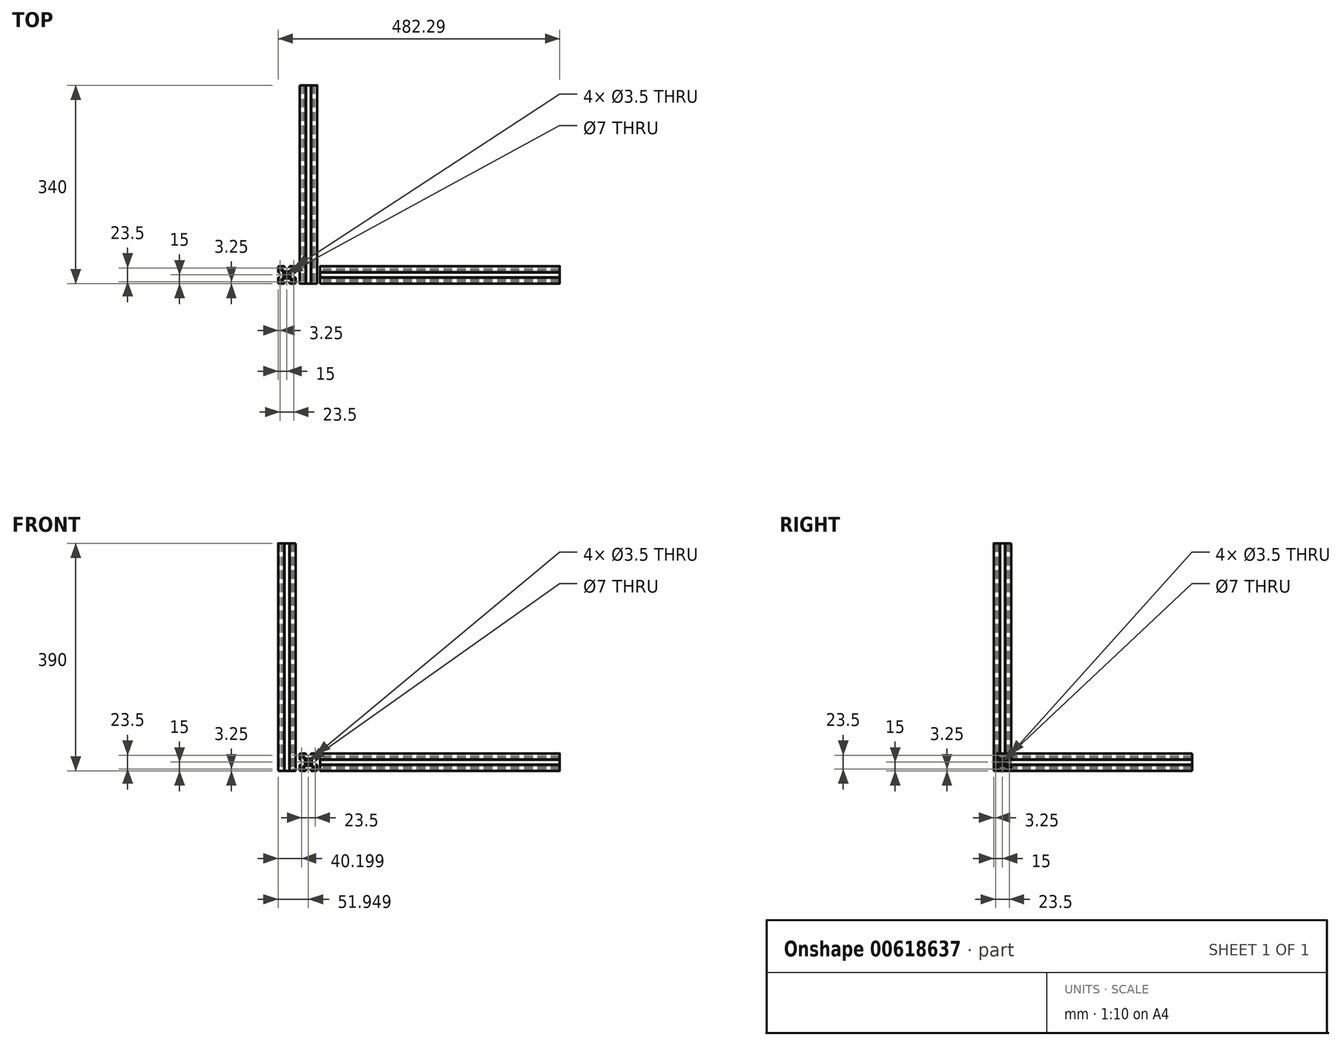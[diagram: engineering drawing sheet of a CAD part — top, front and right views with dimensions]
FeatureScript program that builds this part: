
annotation { "Feature Type Name" : "Feature", "Feature Type Description" : "" }
export const myFeature = defineFeature(function(context is Context, id is Id, definition is map)
    precondition{}
    {
        {
            var Q0;
            Q0=qCreatedBy(makeId("Front.planeOp"),FACE);
            var sketch = newSketch(context, id + "F0", { "sketchPlane" : qUnion([Q0])});
            skLineSegment(sketch, "E0.bottom", {"start": v(-33.34, 30) * mm, "end": v(-25.04, 30) * mm});
            skLineSegment(sketch, "E0.top", {"start": v(-33.34, 0) * mm, "end": v(-25.04, 0) * mm});
            skLineSegment(sketch, "E0.left", {"start": v(-35.34, 28) * mm, "end": v(-35.34, 19.7) * mm});
            skLineSegment(sketch, "E0.right", {"start": v(-5.34, 28) * mm, "end": v(-5.34, 19.7) * mm});
            skPoint(sketch, "E1", {"position": v(-20.34, 15) * mm});
            skLineSegment(sketch, "E2.bottom", {"start": v(-28.84, 27.8) * mm, "end": v(-24.44, 27.8) * mm});
            skLineSegment(sketch, "E2.left", {"start": v(-33.14, 23.5) * mm, "end": v(-33.14, 19.1) * mm});
            skCircle(sketch, "E3", {"center": v(-20.34, 15) * mm, "radius": 3.5 * mm});
            skCircle(sketch, "E4", {"center": v(-32.1, 3.25) * mm, "radius": 1.75 * mm});
            skCircle(sketch, "E5", {"center": v(-32.1, 26.75) * mm, "radius": 1.75 * mm});
            skCircle(sketch, "E6", {"center": v(-8.6, 26.75) * mm, "radius": 1.75 * mm});
            skCircle(sketch, "E7", {"center": v(-8.6, 3.25) * mm, "radius": 1.75 * mm});
            skLineSegment(sketch, "E8.right", {"start": v(-16.24, 2.2) * mm, "end": v(-16.24, 0.5) * mm});
            skLineSegment(sketch, "E9.trimOffspring", {"start": v(-16.24, 2.2) * mm, "end": v(-11.84, 2.2) * mm});
            skLineSegment(sketch, "E10.trimOffspring", {"start": v(-15.64, 0) * mm, "end": v(-7.34, 0) * mm});
            skLineSegment(sketch, "E11.trimOffspring", {"start": v(-24.44, 2.2) * mm, "end": v(-24.44, 0.5) * mm});
            skLineSegment(sketch, "E12.trimOffspring", {"start": v(-28.84, 2.2) * mm, "end": v(-24.44, 2.2) * mm});
            skLineSegment(sketch, "E13.trimOffspring", {"start": v(-7.54, 23.5) * mm, "end": v(-7.54, 19.1) * mm});
            skLineSegment(sketch, "E14", {"start": v(-24.44, 27.8) * mm, "end": v(-24.44, 29.5) * mm});
            skLineSegment(sketch, "E15", {"start": v(-16.24, 27.8) * mm, "end": v(-16.24, 29.5) * mm});
            skLineSegment(sketch, "E16.trimOffspring", {"start": v(-15.64, 30) * mm, "end": v(-7.34, 30) * mm});
            skLineSegment(sketch, "E17.trimOffspring", {"start": v(-16.24, 27.8) * mm, "end": v(-11.84, 27.8) * mm});
            skLineSegment(sketch, "E18", {"start": v(-7.54, 10.9) * mm, "end": v(-5.84, 10.9) * mm});
            skLineSegment(sketch, "E19", {"start": v(-7.54, 19.1) * mm, "end": v(-5.84, 19.1) * mm});
            skLineSegment(sketch, "E20", {"start": v(-33.14, 10.9) * mm, "end": v(-34.84, 10.9) * mm});
            skLineSegment(sketch, "E21", {"start": v(-33.14, 19.1) * mm, "end": v(-34.84, 19.1) * mm});
            skLineSegment(sketch, "E22.trimOffspring", {"start": v(-5.34, 10.3) * mm, "end": v(-5.34, 2) * mm});
            skLineSegment(sketch, "E23.trimOffspring", {"start": v(-7.54, 10.9) * mm, "end": v(-7.54, 6.5) * mm});
            skLineSegment(sketch, "E24.trimOffspring", {"start": v(-33.14, 10.9) * mm, "end": v(-33.14, 6.5) * mm});
            skLineSegment(sketch, "E25.trimOffspring", {"start": v(-35.34, 10.3) * mm, "end": v(-35.34, 2) * mm});
            skLineSegment(sketch, "E26.bottom", {"start": v(-24.93, 21) * mm, "end": v(-15.75, 21) * mm});
            skLineSegment(sketch, "E26.top", {"start": v(-24.93, 9) * mm, "end": v(-15.75, 9) * mm});
            skLineSegment(sketch, "E26.left", {"start": v(-26.34, 19.59) * mm, "end": v(-26.34, 10.41) * mm});
            skLineSegment(sketch, "E26.right", {"start": v(-14.34, 19.59) * mm, "end": v(-14.34, 10.41) * mm});
            skLineSegment(sketch, "E27", {"start": v(-28.84, 27.8) * mm, "end": v(-28.84, 24.91) * mm});
            skLineSegment(sketch, "E28", {"start": v(-30.25, 23.5) * mm, "end": v(-33.14, 23.5) * mm});
            skLineSegment(sketch, "E29", {"start": v(-11.84, 24.91) * mm, "end": v(-11.84, 27.8) * mm});
            skLineSegment(sketch, "E30", {"start": v(-10.43, 23.5) * mm, "end": v(-7.54, 23.5) * mm});
            skLineSegment(sketch, "E31", {"start": v(-10.43, 6.5) * mm, "end": v(-7.54, 6.5) * mm});
            skLineSegment(sketch, "E32", {"start": v(-11.84, 5.09) * mm, "end": v(-11.84, 2.2) * mm});
            skLineSegment(sketch, "E33", {"start": v(-28.84, 5.09) * mm, "end": v(-28.84, 2.2) * mm});
            skLineSegment(sketch, "E34", {"start": v(-30.25, 6.5) * mm, "end": v(-33.14, 6.5) * mm});
            skLineSegment(sketch, "E35", {"start": v(-30.25, 23.5) * mm, "end": v(-26.34, 19.59) * mm});
            skLineSegment(sketch, "E36", {"start": v(-28.84, 24.91) * mm, "end": v(-24.93, 21) * mm});
            skLineSegment(sketch, "E37", {"start": v(-14.34, 10.41) * mm, "end": v(-10.43, 6.5) * mm});
            skLineSegment(sketch, "E38", {"start": v(-15.75, 9) * mm, "end": v(-11.84, 5.09) * mm});
            skLineSegment(sketch, "E39", {"start": v(-28.84, 5.09) * mm, "end": v(-24.93, 9) * mm});
            skLineSegment(sketch, "E40", {"start": v(-30.25, 6.5) * mm, "end": v(-26.34, 10.41) * mm});
            skLineSegment(sketch, "E41", {"start": v(-15.75, 21) * mm, "end": v(-11.84, 24.91) * mm});
            skLineSegment(sketch, "E42", {"start": v(-14.34, 19.59) * mm, "end": v(-10.43, 23.5) * mm});
            skArc(sketch, "E43.filletArc", {"start": v(-33.34, 30) * mm, "mid": v(-34.75, 29.41) * mm, "end": v(-35.34, 28) * mm});
            skArc(sketch, "E44.filletArc", {"start": v(-5.34, 28) * mm, "mid": v(-5.93, 29.41) * mm, "end": v(-7.34, 30) * mm});
            skArc(sketch, "E45.filletArc", {"start": v(-7.34, 0) * mm, "mid": v(-5.93, 0.59) * mm, "end": v(-5.34, 2) * mm});
            skArc(sketch, "E46.filletArc", {"start": v(-35.34, 2) * mm, "mid": v(-34.75, 0.59) * mm, "end": v(-33.34, 0) * mm});
            skLineSegment(sketch, "E47", {"start": v(-5.84, 19.1) * mm, "end": v(-5.84, 19.7) * mm});
            skLineSegment(sketch, "E48", {"start": v(-5.84, 19.7) * mm, "end": v(-5.34, 19.7) * mm});
            skLineSegment(sketch, "E49.top", {"start": v(-5.34, 10.3) * mm, "end": v(-5.84, 10.3) * mm});
            skLineSegment(sketch, "E49.right", {"start": v(-5.84, 10.9) * mm, "end": v(-5.84, 10.3) * mm});
            skLineSegment(sketch, "E50.top", {"start": v(-16.24, 0.5) * mm, "end": v(-15.64, 0.5) * mm});
            skLineSegment(sketch, "E50.right", {"start": v(-15.64, 0) * mm, "end": v(-15.64, 0.5) * mm});
            skLineSegment(sketch, "E51.top", {"start": v(-24.44, 0.5) * mm, "end": v(-25.04, 0.5) * mm});
            skLineSegment(sketch, "E51.right", {"start": v(-25.04, 0) * mm, "end": v(-25.04, 0.5) * mm});
            skLineSegment(sketch, "E52.top", {"start": v(-35.34, 10.3) * mm, "end": v(-34.84, 10.3) * mm});
            skLineSegment(sketch, "E52.right", {"start": v(-34.84, 10.9) * mm, "end": v(-34.84, 10.3) * mm});
            skLineSegment(sketch, "E53.top", {"start": v(-35.34, 19.7) * mm, "end": v(-34.84, 19.7) * mm});
            skLineSegment(sketch, "E53.right", {"start": v(-34.84, 19.1) * mm, "end": v(-34.84, 19.7) * mm});
            skLineSegment(sketch, "E54.top", {"start": v(-24.44, 29.5) * mm, "end": v(-25.04, 29.5) * mm});
            skLineSegment(sketch, "E54.right", {"start": v(-25.04, 30) * mm, "end": v(-25.04, 29.5) * mm});
            skLineSegment(sketch, "E55.top", {"start": v(-16.24, 29.5) * mm, "end": v(-15.64, 29.5) * mm});
            skLineSegment(sketch, "E55.right", {"start": v(-15.64, 30) * mm, "end": v(-15.64, 29.5) * mm});
            skSolve(sketch);
        }
        {
            var Q0;
            Q0 = qSketchRegion(id + "F0", true);
            extrude(context, id + "F1", {"entities" : qUnion([Q0]), "oppositeDirection" : true, "depth" : 340 * mm, "offsetDistance" : 25 * mm});
        }
        {
            var Q0;
            Q0=qCreatedBy(makeId("Top.planeOp"),FACE);
            var sketch = newSketch(context, id + "F2", { "sketchPlane" : qUnion([Q0])});
            skLineSegment(sketch, "E56.bottom", {"start": v(-70.29, 30) * mm, "end": v(-61.99, 30) * mm});
            skLineSegment(sketch, "E56.top", {"start": v(-70.29, 0) * mm, "end": v(-61.99, 0) * mm});
            skLineSegment(sketch, "E56.left", {"start": v(-72.29, 28) * mm, "end": v(-72.29, 19.7) * mm});
            skLineSegment(sketch, "E56.right", {"start": v(-42.29, 28) * mm, "end": v(-42.29, 19.7) * mm});
            skPoint(sketch, "E57", {"position": v(-57.29, 15) * mm});
            skLineSegment(sketch, "E58.bottom", {"start": v(-65.79, 27.8) * mm, "end": v(-61.39, 27.8) * mm});
            skLineSegment(sketch, "E58.left", {"start": v(-70.09, 23.5) * mm, "end": v(-70.09, 19.1) * mm});
            skCircle(sketch, "E59", {"center": v(-57.29, 15) * mm, "radius": 3.5 * mm});
            skCircle(sketch, "E60", {"center": v(-69.04, 3.25) * mm, "radius": 1.75 * mm});
            skCircle(sketch, "E61", {"center": v(-69.04, 26.75) * mm, "radius": 1.75 * mm});
            skCircle(sketch, "E62", {"center": v(-45.54, 26.75) * mm, "radius": 1.75 * mm});
            skCircle(sketch, "E63", {"center": v(-45.54, 3.25) * mm, "radius": 1.75 * mm});
            skLineSegment(sketch, "E64.right", {"start": v(-53.19, 2.2) * mm, "end": v(-53.19, 0.5) * mm});
            skLineSegment(sketch, "E65.trimOffspring", {"start": v(-53.19, 2.2) * mm, "end": v(-48.79, 2.2) * mm});
            skLineSegment(sketch, "E66.trimOffspring", {"start": v(-52.59, 0) * mm, "end": v(-44.29, 0) * mm});
            skLineSegment(sketch, "E67.trimOffspring", {"start": v(-61.39, 2.2) * mm, "end": v(-61.39, 0.5) * mm});
            skLineSegment(sketch, "E68.trimOffspring", {"start": v(-65.79, 2.2) * mm, "end": v(-61.39, 2.2) * mm});
            skLineSegment(sketch, "E69.trimOffspring", {"start": v(-44.49, 23.5) * mm, "end": v(-44.49, 19.1) * mm});
            skLineSegment(sketch, "E70", {"start": v(-61.39, 27.8) * mm, "end": v(-61.39, 29.5) * mm});
            skLineSegment(sketch, "E71", {"start": v(-53.19, 27.8) * mm, "end": v(-53.19, 29.5) * mm});
            skLineSegment(sketch, "E72.trimOffspring", {"start": v(-52.59, 30) * mm, "end": v(-44.29, 30) * mm});
            skLineSegment(sketch, "E73.trimOffspring", {"start": v(-53.19, 27.8) * mm, "end": v(-48.79, 27.8) * mm});
            skLineSegment(sketch, "E74", {"start": v(-44.49, 10.9) * mm, "end": v(-42.79, 10.9) * mm});
            skLineSegment(sketch, "E75", {"start": v(-44.49, 19.1) * mm, "end": v(-42.79, 19.1) * mm});
            skLineSegment(sketch, "E76", {"start": v(-70.09, 10.9) * mm, "end": v(-71.79, 10.9) * mm});
            skLineSegment(sketch, "E77", {"start": v(-70.09, 19.1) * mm, "end": v(-71.79, 19.1) * mm});
            skLineSegment(sketch, "E78.trimOffspring", {"start": v(-42.29, 10.3) * mm, "end": v(-42.29, 2) * mm});
            skLineSegment(sketch, "E79.trimOffspring", {"start": v(-44.49, 10.9) * mm, "end": v(-44.49, 6.5) * mm});
            skLineSegment(sketch, "E80.trimOffspring", {"start": v(-70.09, 10.9) * mm, "end": v(-70.09, 6.5) * mm});
            skLineSegment(sketch, "E81.trimOffspring", {"start": v(-72.29, 10.3) * mm, "end": v(-72.29, 2) * mm});
            skLineSegment(sketch, "E82.bottom", {"start": v(-61.88, 21) * mm, "end": v(-52.7, 21) * mm});
            skLineSegment(sketch, "E82.top", {"start": v(-61.88, 9) * mm, "end": v(-52.7, 9) * mm});
            skLineSegment(sketch, "E82.left", {"start": v(-63.29, 19.59) * mm, "end": v(-63.29, 10.41) * mm});
            skLineSegment(sketch, "E82.right", {"start": v(-51.29, 19.59) * mm, "end": v(-51.29, 10.41) * mm});
            skLineSegment(sketch, "E83", {"start": v(-65.79, 27.8) * mm, "end": v(-65.79, 24.91) * mm});
            skLineSegment(sketch, "E84", {"start": v(-67.2, 23.5) * mm, "end": v(-70.09, 23.5) * mm});
            skLineSegment(sketch, "E85", {"start": v(-48.79, 24.91) * mm, "end": v(-48.79, 27.8) * mm});
            skLineSegment(sketch, "E86", {"start": v(-47.38, 23.5) * mm, "end": v(-44.49, 23.5) * mm});
            skLineSegment(sketch, "E87", {"start": v(-47.38, 6.5) * mm, "end": v(-44.49, 6.5) * mm});
            skLineSegment(sketch, "E88", {"start": v(-48.79, 5.09) * mm, "end": v(-48.79, 2.2) * mm});
            skLineSegment(sketch, "E89", {"start": v(-65.79, 5.09) * mm, "end": v(-65.79, 2.2) * mm});
            skLineSegment(sketch, "E90", {"start": v(-67.2, 6.5) * mm, "end": v(-70.09, 6.5) * mm});
            skLineSegment(sketch, "E91", {"start": v(-67.2, 23.5) * mm, "end": v(-63.29, 19.59) * mm});
            skLineSegment(sketch, "E92", {"start": v(-65.79, 24.91) * mm, "end": v(-61.88, 21) * mm});
            skLineSegment(sketch, "E93", {"start": v(-51.29, 10.41) * mm, "end": v(-47.38, 6.5) * mm});
            skLineSegment(sketch, "E94", {"start": v(-52.7, 9) * mm, "end": v(-48.79, 5.09) * mm});
            skLineSegment(sketch, "E95", {"start": v(-65.79, 5.09) * mm, "end": v(-61.88, 9) * mm});
            skLineSegment(sketch, "E96", {"start": v(-67.2, 6.5) * mm, "end": v(-63.29, 10.41) * mm});
            skLineSegment(sketch, "E97", {"start": v(-52.7, 21) * mm, "end": v(-48.79, 24.91) * mm});
            skLineSegment(sketch, "E98", {"start": v(-51.29, 19.59) * mm, "end": v(-47.38, 23.5) * mm});
            skArc(sketch, "E99.filletArc", {"start": v(-70.29, 30) * mm, "mid": v(-71.7, 29.41) * mm, "end": v(-72.29, 28) * mm});
            skArc(sketch, "E100.filletArc", {"start": v(-42.29, 28) * mm, "mid": v(-42.88, 29.41) * mm, "end": v(-44.29, 30) * mm});
            skArc(sketch, "E101.filletArc", {"start": v(-44.29, 0) * mm, "mid": v(-42.88, 0.59) * mm, "end": v(-42.29, 2) * mm});
            skArc(sketch, "E102.filletArc", {"start": v(-72.29, 2) * mm, "mid": v(-71.7, 0.59) * mm, "end": v(-70.29, 0) * mm});
            skLineSegment(sketch, "E103", {"start": v(-42.79, 19.1) * mm, "end": v(-42.79, 19.7) * mm});
            skLineSegment(sketch, "E104", {"start": v(-42.79, 19.7) * mm, "end": v(-42.29, 19.7) * mm});
            skLineSegment(sketch, "E105.top", {"start": v(-42.29, 10.3) * mm, "end": v(-42.79, 10.3) * mm});
            skLineSegment(sketch, "E105.right", {"start": v(-42.79, 10.9) * mm, "end": v(-42.79, 10.3) * mm});
            skLineSegment(sketch, "E106.top", {"start": v(-53.19, 0.5) * mm, "end": v(-52.59, 0.5) * mm});
            skLineSegment(sketch, "E106.right", {"start": v(-52.59, 0) * mm, "end": v(-52.59, 0.5) * mm});
            skLineSegment(sketch, "E107.top", {"start": v(-61.39, 0.5) * mm, "end": v(-61.99, 0.5) * mm});
            skLineSegment(sketch, "E107.right", {"start": v(-61.99, 0) * mm, "end": v(-61.99, 0.5) * mm});
            skLineSegment(sketch, "E108.top", {"start": v(-72.29, 10.3) * mm, "end": v(-71.79, 10.3) * mm});
            skLineSegment(sketch, "E108.right", {"start": v(-71.79, 10.9) * mm, "end": v(-71.79, 10.3) * mm});
            skLineSegment(sketch, "E109.top", {"start": v(-72.29, 19.7) * mm, "end": v(-71.79, 19.7) * mm});
            skLineSegment(sketch, "E109.right", {"start": v(-71.79, 19.1) * mm, "end": v(-71.79, 19.7) * mm});
            skLineSegment(sketch, "E110.top", {"start": v(-61.39, 29.5) * mm, "end": v(-61.99, 29.5) * mm});
            skLineSegment(sketch, "E110.right", {"start": v(-61.99, 30) * mm, "end": v(-61.99, 29.5) * mm});
            skLineSegment(sketch, "E111.top", {"start": v(-53.19, 29.5) * mm, "end": v(-52.59, 29.5) * mm});
            skLineSegment(sketch, "E111.right", {"start": v(-52.59, 30) * mm, "end": v(-52.59, 29.5) * mm});
            skSolve(sketch);
        }
        {
            var Q0;
            Q0 = qSketchRegion(id + "F2", true);
            extrude(context, id + "F3", {"entities" : qUnion([Q0]), "depth" : 390 * mm, "offsetDistance" : 25 * mm});
        }
        {
            var Q0;
            Q0=qCreatedBy(makeId("Right.planeOp"),FACE);
            var sketch = newSketch(context, id + "F4", { "sketchPlane" : qUnion([Q0])});
            skLineSegment(sketch, "E112.bottom", {"start": v(2, 30) * mm, "end": v(10.3, 30) * mm});
            skLineSegment(sketch, "E112.top", {"start": v(2, 0) * mm, "end": v(10.3, 0) * mm});
            skLineSegment(sketch, "E112.left", {"start": v(0, 28) * mm, "end": v(0, 19.7) * mm});
            skLineSegment(sketch, "E112.right", {"start": v(30, 28) * mm, "end": v(30, 19.7) * mm});
            skPoint(sketch, "E113", {"position": v(15, 15) * mm});
            skLineSegment(sketch, "E114.bottom", {"start": v(6.5, 27.8) * mm, "end": v(10.9, 27.8) * mm});
            skLineSegment(sketch, "E114.left", {"start": v(2.2, 23.5) * mm, "end": v(2.2, 19.1) * mm});
            skCircle(sketch, "E115", {"center": v(15, 15) * mm, "radius": 3.5 * mm});
            skCircle(sketch, "E116", {"center": v(3.25, 3.25) * mm, "radius": 1.75 * mm});
            skCircle(sketch, "E117", {"center": v(3.25, 26.75) * mm, "radius": 1.75 * mm});
            skCircle(sketch, "E118", {"center": v(26.75, 26.75) * mm, "radius": 1.75 * mm});
            skCircle(sketch, "E119", {"center": v(26.75, 3.25) * mm, "radius": 1.75 * mm});
            skLineSegment(sketch, "E120.right", {"start": v(19.1, 2.2) * mm, "end": v(19.1, 0.5) * mm});
            skLineSegment(sketch, "E121.trimOffspring", {"start": v(19.1, 2.2) * mm, "end": v(23.5, 2.2) * mm});
            skLineSegment(sketch, "E122.trimOffspring", {"start": v(19.7, 0) * mm, "end": v(28, 0) * mm});
            skLineSegment(sketch, "E123.trimOffspring", {"start": v(10.9, 2.2) * mm, "end": v(10.9, 0.5) * mm});
            skLineSegment(sketch, "E124.trimOffspring", {"start": v(6.5, 2.2) * mm, "end": v(10.9, 2.2) * mm});
            skLineSegment(sketch, "E125.trimOffspring", {"start": v(27.8, 23.5) * mm, "end": v(27.8, 19.1) * mm});
            skLineSegment(sketch, "E126", {"start": v(10.9, 27.8) * mm, "end": v(10.9, 29.5) * mm});
            skLineSegment(sketch, "E127", {"start": v(19.1, 27.8) * mm, "end": v(19.1, 29.5) * mm});
            skLineSegment(sketch, "E128.trimOffspring", {"start": v(19.7, 30) * mm, "end": v(28, 30) * mm});
            skLineSegment(sketch, "E129.trimOffspring", {"start": v(19.1, 27.8) * mm, "end": v(23.5, 27.8) * mm});
            skLineSegment(sketch, "E130", {"start": v(27.8, 10.9) * mm, "end": v(29.5, 10.9) * mm});
            skLineSegment(sketch, "E131", {"start": v(27.8, 19.1) * mm, "end": v(29.5, 19.1) * mm});
            skLineSegment(sketch, "E132", {"start": v(2.2, 10.9) * mm, "end": v(0.5, 10.9) * mm});
            skLineSegment(sketch, "E133", {"start": v(2.2, 19.1) * mm, "end": v(0.5, 19.1) * mm});
            skLineSegment(sketch, "E134.trimOffspring", {"start": v(30, 10.3) * mm, "end": v(30, 2) * mm});
            skLineSegment(sketch, "E135.trimOffspring", {"start": v(27.8, 10.9) * mm, "end": v(27.8, 6.5) * mm});
            skLineSegment(sketch, "E136.trimOffspring", {"start": v(2.2, 10.9) * mm, "end": v(2.2, 6.5) * mm});
            skLineSegment(sketch, "E137.trimOffspring", {"start": v(0, 10.3) * mm, "end": v(0, 2) * mm});
            skLineSegment(sketch, "E138.bottom", {"start": v(10.41, 21) * mm, "end": v(19.59, 21) * mm});
            skLineSegment(sketch, "E138.top", {"start": v(10.41, 9) * mm, "end": v(19.59, 9) * mm});
            skLineSegment(sketch, "E138.left", {"start": v(9, 19.59) * mm, "end": v(9, 10.41) * mm});
            skLineSegment(sketch, "E138.right", {"start": v(21, 19.59) * mm, "end": v(21, 10.41) * mm});
            skLineSegment(sketch, "E139", {"start": v(6.5, 27.8) * mm, "end": v(6.5, 24.91) * mm});
            skLineSegment(sketch, "E140", {"start": v(5.09, 23.5) * mm, "end": v(2.2, 23.5) * mm});
            skLineSegment(sketch, "E141", {"start": v(23.5, 24.91) * mm, "end": v(23.5, 27.8) * mm});
            skLineSegment(sketch, "E142", {"start": v(24.91, 23.5) * mm, "end": v(27.8, 23.5) * mm});
            skLineSegment(sketch, "E143", {"start": v(24.91, 6.5) * mm, "end": v(27.8, 6.5) * mm});
            skLineSegment(sketch, "E144", {"start": v(23.5, 5.09) * mm, "end": v(23.5, 2.2) * mm});
            skLineSegment(sketch, "E145", {"start": v(6.5, 5.09) * mm, "end": v(6.5, 2.2) * mm});
            skLineSegment(sketch, "E146", {"start": v(5.09, 6.5) * mm, "end": v(2.2, 6.5) * mm});
            skLineSegment(sketch, "E147", {"start": v(5.09, 23.5) * mm, "end": v(9, 19.59) * mm});
            skLineSegment(sketch, "E148", {"start": v(6.5, 24.91) * mm, "end": v(10.41, 21) * mm});
            skLineSegment(sketch, "E149", {"start": v(21, 10.41) * mm, "end": v(24.91, 6.5) * mm});
            skLineSegment(sketch, "E150", {"start": v(19.59, 9) * mm, "end": v(23.5, 5.09) * mm});
            skLineSegment(sketch, "E151", {"start": v(6.5, 5.09) * mm, "end": v(10.41, 9) * mm});
            skLineSegment(sketch, "E152", {"start": v(5.09, 6.5) * mm, "end": v(9, 10.41) * mm});
            skLineSegment(sketch, "E153", {"start": v(19.59, 21) * mm, "end": v(23.5, 24.91) * mm});
            skLineSegment(sketch, "E154", {"start": v(21, 19.59) * mm, "end": v(24.91, 23.5) * mm});
            skArc(sketch, "E155.filletArc", {"start": v(2, 30) * mm, "mid": v(0.59, 29.41) * mm, "end": v(0, 28) * mm});
            skArc(sketch, "E156.filletArc", {"start": v(30, 28) * mm, "mid": v(29.41, 29.41) * mm, "end": v(28, 30) * mm});
            skArc(sketch, "E157.filletArc", {"start": v(28, 0) * mm, "mid": v(29.41, 0.59) * mm, "end": v(30, 2) * mm});
            skArc(sketch, "E158.filletArc", {"start": v(0, 2) * mm, "mid": v(0.59, 0.59) * mm, "end": v(2, 0) * mm});
            skLineSegment(sketch, "E159", {"start": v(29.5, 19.1) * mm, "end": v(29.5, 19.7) * mm});
            skLineSegment(sketch, "E160", {"start": v(29.5, 19.7) * mm, "end": v(30, 19.7) * mm});
            skLineSegment(sketch, "E161.top", {"start": v(30, 10.3) * mm, "end": v(29.5, 10.3) * mm});
            skLineSegment(sketch, "E161.right", {"start": v(29.5, 10.9) * mm, "end": v(29.5, 10.3) * mm});
            skLineSegment(sketch, "E162.top", {"start": v(19.1, 0.5) * mm, "end": v(19.7, 0.5) * mm});
            skLineSegment(sketch, "E162.right", {"start": v(19.7, 0) * mm, "end": v(19.7, 0.5) * mm});
            skLineSegment(sketch, "E163.top", {"start": v(10.9, 0.5) * mm, "end": v(10.3, 0.5) * mm});
            skLineSegment(sketch, "E163.right", {"start": v(10.3, 0) * mm, "end": v(10.3, 0.5) * mm});
            skLineSegment(sketch, "E164.top", {"start": v(0, 10.3) * mm, "end": v(0.5, 10.3) * mm});
            skLineSegment(sketch, "E164.right", {"start": v(0.5, 10.9) * mm, "end": v(0.5, 10.3) * mm});
            skLineSegment(sketch, "E165.top", {"start": v(0, 19.7) * mm, "end": v(0.5, 19.7) * mm});
            skLineSegment(sketch, "E165.right", {"start": v(0.5, 19.1) * mm, "end": v(0.5, 19.7) * mm});
            skLineSegment(sketch, "E166.top", {"start": v(10.9, 29.5) * mm, "end": v(10.3, 29.5) * mm});
            skLineSegment(sketch, "E166.right", {"start": v(10.3, 30) * mm, "end": v(10.3, 29.5) * mm});
            skLineSegment(sketch, "E167.top", {"start": v(19.1, 29.5) * mm, "end": v(19.7, 29.5) * mm});
            skLineSegment(sketch, "E167.right", {"start": v(19.7, 30) * mm, "end": v(19.7, 29.5) * mm});
            skSolve(sketch);
        }
        {
            var Q0;
            Q0 = qSketchRegion(id + "F4", true);
            extrude(context, id + "F5", {"entities" : qUnion([Q0]), "depth" : 410 * mm, "offsetDistance" : 25 * mm});
        }
    });
